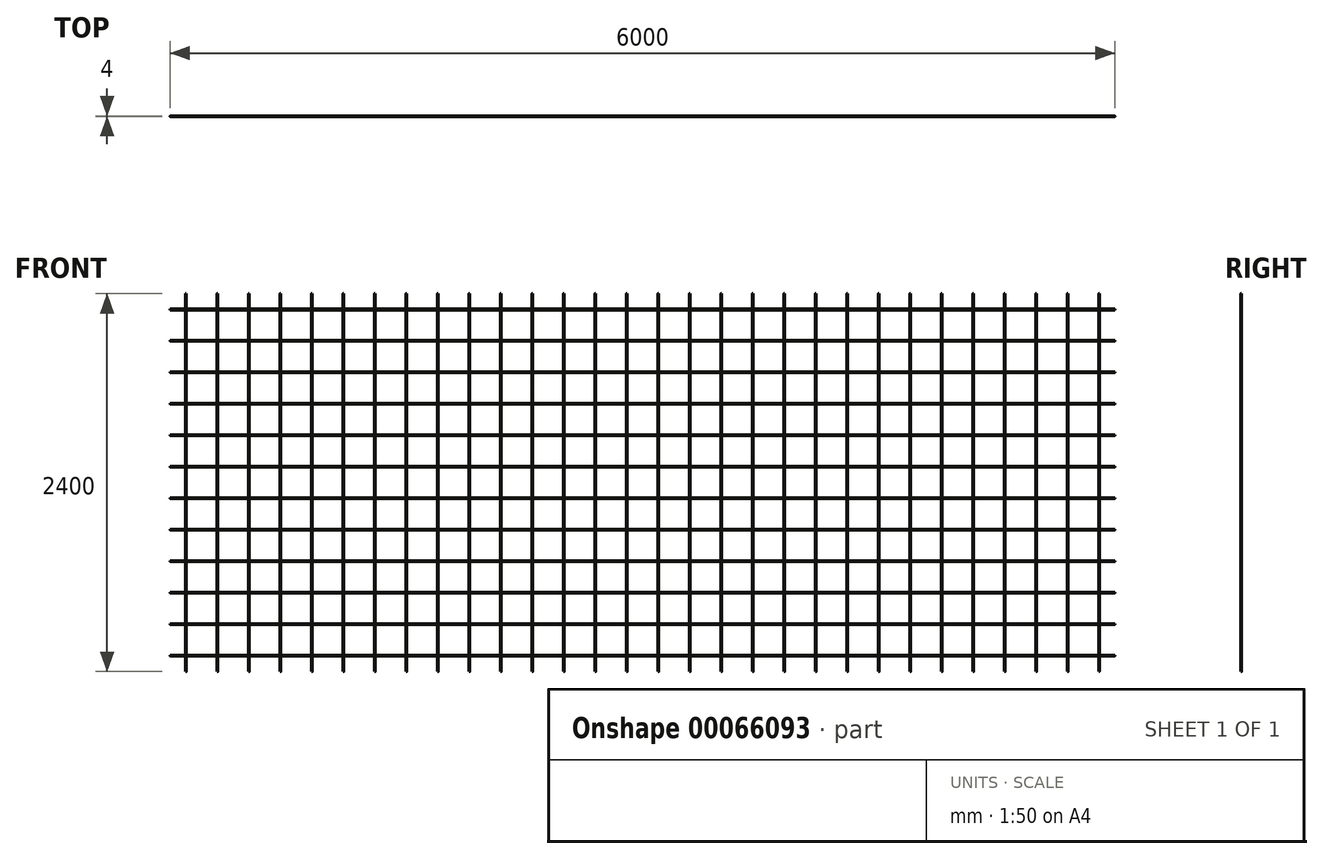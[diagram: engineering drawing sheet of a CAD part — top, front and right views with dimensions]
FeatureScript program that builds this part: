
annotation { "Feature Type Name" : "Feature", "Feature Type Description" : "" }
export const myFeature = defineFeature(function(context is Context, id is Id, definition is map)
    precondition{}
    {
        {
            var Q0;
            Q0=qCreatedBy(makeId("Top.planeOp"),FACE);
            var sketch = newSketch(context, id + "F0", { "sketchPlane" : qUnion([Q0])});
            skCircle(sketch, "E0", {"center": v(0, 0) * mm, "radius": 2 * mm});
            skCircle(sketch, "E1.1.0.0", {"center": v(200, 0) * mm, "radius": 2 * mm});
            skCircle(sketch, "E1.2.0.0", {"center": v(400, 0) * mm, "radius": 2 * mm});
            skCircle(sketch, "E1.3.0.0", {"center": v(600, 0) * mm, "radius": 2 * mm});
            skCircle(sketch, "E1.4.0.0", {"center": v(800, 0) * mm, "radius": 2 * mm});
            skCircle(sketch, "E1.5.0.0", {"center": v(1000, 0) * mm, "radius": 2 * mm});
            skCircle(sketch, "E1.6.0.0", {"center": v(1200, 0) * mm, "radius": 2 * mm});
            skCircle(sketch, "E1.7.0.0", {"center": v(1400, 0) * mm, "radius": 2 * mm});
            skCircle(sketch, "E1.8.0.0", {"center": v(1600, 0) * mm, "radius": 2 * mm});
            skCircle(sketch, "E1.9.0.0", {"center": v(1800, 0) * mm, "radius": 2 * mm});
            skCircle(sketch, "E1.10.0.0", {"center": v(2000, 0) * mm, "radius": 2 * mm});
            skLineSegment(sketch, "E1.direction1", {"start": v(0, 0) * mm, "end": v(200, 0) * mm, "construction": true});
            skCircle(sketch, "E2.0.11.0", {"center": v(2200, 0) * mm, "radius": 2 * mm});
            skCircle(sketch, "E2.0.12.0", {"center": v(2400, 0) * mm, "radius": 2 * mm});
            skCircle(sketch, "E2.0.13.0", {"center": v(2600, 0) * mm, "radius": 2 * mm});
            skCircle(sketch, "E2.0.14.0", {"center": v(2800, 0) * mm, "radius": 2 * mm});
            skCircle(sketch, "E2.0.15.0", {"center": v(3000, 0) * mm, "radius": 2 * mm});
            skCircle(sketch, "E2.0.16.0", {"center": v(3200, 0) * mm, "radius": 2 * mm});
            skCircle(sketch, "E2.0.17.0", {"center": v(3400, 0) * mm, "radius": 2 * mm});
            skCircle(sketch, "E2.0.18.0", {"center": v(3600, 0) * mm, "radius": 2 * mm});
            skCircle(sketch, "E2.0.19.0", {"center": v(3800, 0) * mm, "radius": 2 * mm});
            skCircle(sketch, "E2.0.20.0", {"center": v(4000, 0) * mm, "radius": 2 * mm});
            skCircle(sketch, "E2.0.21.0", {"center": v(4200, 0) * mm, "radius": 2 * mm});
            skCircle(sketch, "E2.0.22.0", {"center": v(4400, 0) * mm, "radius": 2 * mm});
            skCircle(sketch, "E2.0.23.0", {"center": v(4600, 0) * mm, "radius": 2 * mm});
            skCircle(sketch, "E2.0.24.0", {"center": v(4800, 0) * mm, "radius": 2 * mm});
            skCircle(sketch, "E2.0.25.0", {"center": v(5000, 0) * mm, "radius": 2 * mm});
            skCircle(sketch, "E2.0.26.0", {"center": v(5200, 0) * mm, "radius": 2 * mm});
            skCircle(sketch, "E2.0.27.0", {"center": v(5400, 0) * mm, "radius": 2 * mm});
            skCircle(sketch, "E2.0.28.0", {"center": v(5600, 0) * mm, "radius": 2 * mm});
            skCircle(sketch, "E3.0.29.0", {"center": v(5800, 0) * mm, "radius": 2 * mm});
            skSolve(sketch);
        }
        {
            var Q0;
            Q0 = qSketchRegion(id + "F0", true);
            extrude(context, id + "F1", {"entities" : qUnion([Q0]), "depth" : 2400 * mm});
        }
        {
            var Q0;
            Q0=qCreatedBy(makeId("Right.planeOp"),FACE);
            var sketch = newSketch(context, id + "F2", { "sketchPlane" : qUnion([Q0])});
            skCircle(sketch, "E4", {"center": v(0, 100) * mm, "radius": 2 * mm});
            skCircle(sketch, "E5.0.1.0", {"center": v(0, 300) * mm, "radius": 2 * mm});
            skCircle(sketch, "E5.0.2.0", {"center": v(0, 500) * mm, "radius": 2 * mm});
            skCircle(sketch, "E5.0.3.0", {"center": v(0, 700) * mm, "radius": 2 * mm});
            skCircle(sketch, "E5.0.4.0", {"center": v(0, 900) * mm, "radius": 2 * mm});
            skCircle(sketch, "E5.0.5.0", {"center": v(0, 1100) * mm, "radius": 2 * mm});
            skCircle(sketch, "E5.0.6.0", {"center": v(0, 1300) * mm, "radius": 2 * mm});
            skCircle(sketch, "E5.0.7.0", {"center": v(0, 1500) * mm, "radius": 2 * mm});
            skCircle(sketch, "E5.0.8.0", {"center": v(0, 1700) * mm, "radius": 2 * mm});
            skCircle(sketch, "E5.0.9.0", {"center": v(0, 1900) * mm, "radius": 2 * mm});
            skCircle(sketch, "E5.0.10.0", {"center": v(0, 2100) * mm, "radius": 2 * mm});
            skLineSegment(sketch, "E5.direction1", {"start": v(0, 100) * mm, "end": v(25, 100) * mm, "construction": true});
            skLineSegment(sketch, "E5.direction2", {"start": v(0, 100) * mm, "end": v(0, 300) * mm, "construction": true});
            skCircle(sketch, "E6.0.0.11", {"center": v(0, 2300) * mm, "radius": 2 * mm});
            skSolve(sketch);
        }
        {
            var Q0;
            Q0 = qSketchRegion(id + "F2", true);
            extrude(context, id + "F3", {"entities" : qUnion([Q0]), "oppositeDirection" : true, "depth" : 100 * mm, "hasSecondDirection" : true, "secondDirectionOppositeDirection" : false, "secondDirectionDepth" : 5900 * mm});
        }
    });
